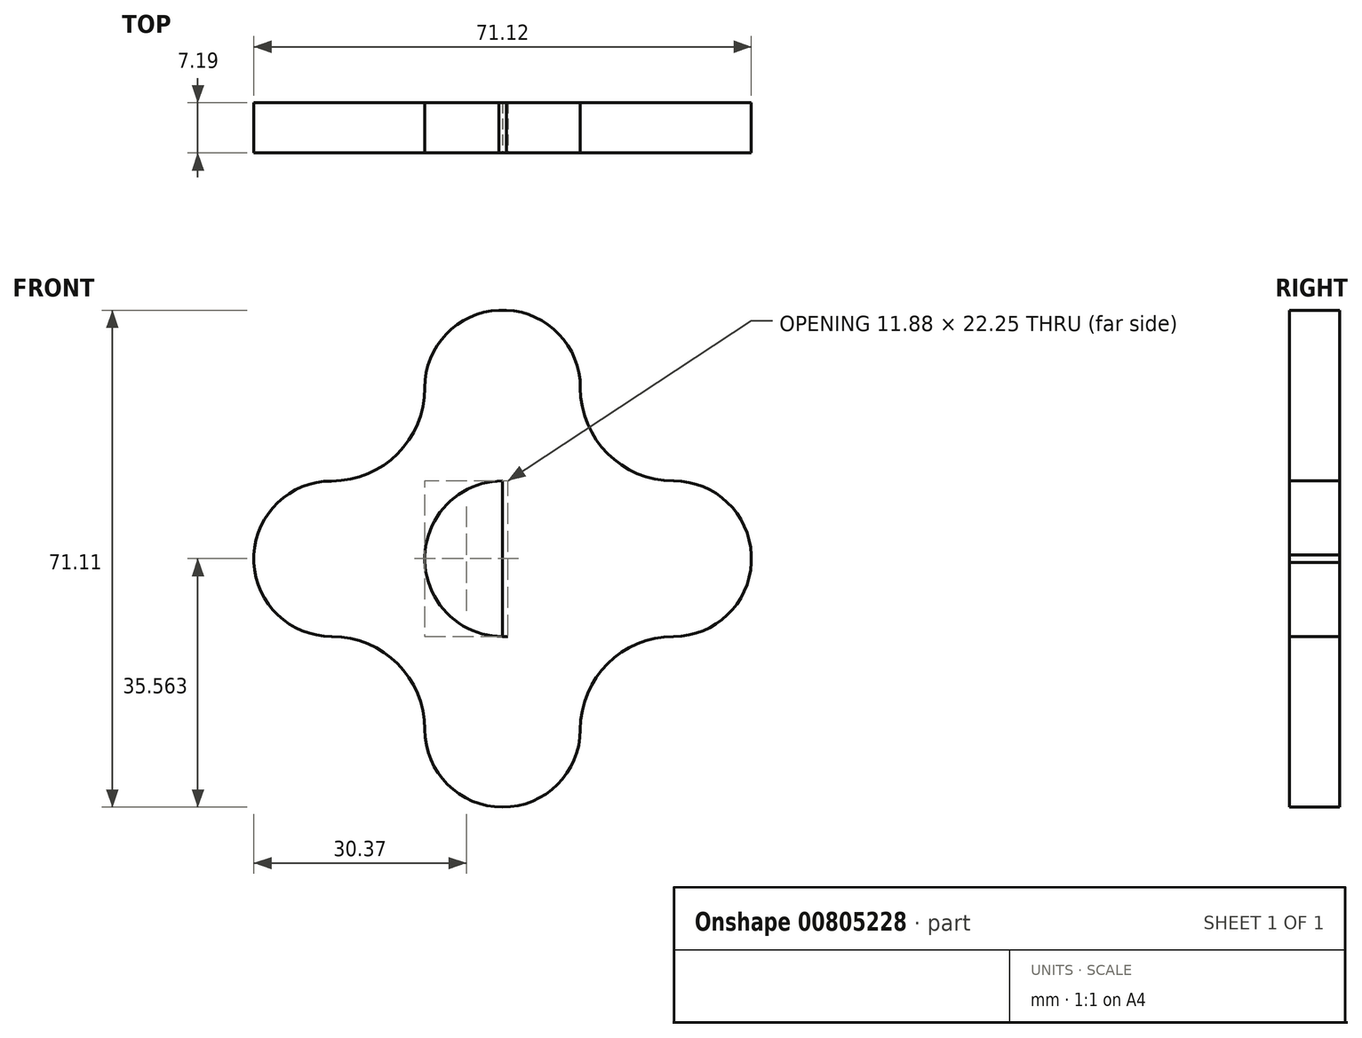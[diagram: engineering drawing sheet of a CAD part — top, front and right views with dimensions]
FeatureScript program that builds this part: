
annotation { "Feature Type Name" : "Feature", "Feature Type Description" : "" }
export const myFeature = defineFeature(function(context is Context, id is Id, definition is map)
    precondition{}
    {
        {
            var Q0;
            Q0=qCreatedBy(makeId("Front.planeOp"),FACE);
            var sketch = newSketch(context, id + "F0", { "sketchPlane" : qUnion([Q0])});
            skCircle(sketch, "E0", {"center": v(0, 0) * mm, "radius": 35.56 * mm});
            skSolve(sketch);
        }
        {
            var Q0;
            Q0=makeQuery(id+"F0.imprint","IMPRINT",FACE,{"disambiguationData":[TD([[makeQuery(id+"F0.imprint","IMPRINT",EDGE,{"derivedFrom":sQuery(id+"F0.wireOp",EDGE,"E0")}),1.0]])]});
            extrude(context, id + "F1", {"entities" : qUnion([Q0]), "depth" : 7.2 * mm, "offsetDistance" : 25.4 * mm});
        }
        {
            var Q0;
            Q0=makeQuery(id+"F1.opExtrude","CAP_FACE",FACE,{"disambiguationData":[OSD([sQuery(id+"F0.wireOp",EDGE,"E0")])],"isStart":true});
            var sketch = newSketch(context, id + "F2", { "sketchPlane" : qUnion([Q0])});
            skCircle(sketch, "E1", {"center": v(0, 0) * mm, "radius": 11.14 * mm});
            skSolve(sketch);
        }
        {
            var Q0;
            Q0=makeQuery(id+"F2.imprint","IMPRINT",FACE,{"disambiguationData":[TD([[makeQuery(id+"F2.imprint","IMPRINT",EDGE,{"derivedFrom":sQuery(id+"F2.wireOp",EDGE,"E1")}),1.0]])]});
            extrude(context, id + "F3", {"entities" : qUnion([Q0]), "operationType" : NewBodyOperationType.REMOVE, "oppositeDirection" : true, "depth" : 7.62 * mm, "offsetDistance" : 25.4 * mm});
        }
        {
            var Q0;
            Q0=makeQuery(id+"F1.opExtrude","CAP_FACE",FACE,{"disambiguationData":[OSD([sQuery(id+"F0.wireOp",EDGE,"E0")])],"isStart":false});
            var sketch = newSketch(context, id + "F4", { "sketchPlane" : qUnion([Q0])});
            skLineSegment(sketch, "E2", {"start": v(0, 35.56) * mm, "end": v(35.56, 0) * mm});
            skLineSegment(sketch, "E3", {"start": v(35.56, 0) * mm, "end": v(0, -35.56) * mm});
            skLineSegment(sketch, "E4", {"start": v(0, -35.56) * mm, "end": v(-35.56, 0) * mm});
            skLineSegment(sketch, "E5", {"start": v(-35.56, 0) * mm, "end": v(0, 35.56) * mm});
            skSolve(sketch);
        }
        {
            var Q0;
            {var subQ0=sQuery(id+"F4.wireOp",EDGE,"E4");Q0=makeQuery(id+"F4.imprint","IMPRINT",FACE,{"disambiguationData":[TD([[makeQuery(id+"F4.imprint","IMPRINT",EDGE,{"derivedFrom":subQ0}),1.0]])]});}
            var Q1;
            {var subQ0=sQuery(id+"F4.wireOp",EDGE,"E5");Q1=makeQuery(id+"F4.imprint","IMPRINT",FACE,{"disambiguationData":[TD([[makeQuery(id+"F4.imprint","IMPRINT",EDGE,{"derivedFrom":subQ0}),1.0]])]});}
            var Q2;
            {var subQ0=sQuery(id+"F4.wireOp",EDGE,"E2");Q2=makeQuery(id+"F4.imprint","IMPRINT",FACE,{"disambiguationData":[TD([[makeQuery(id+"F4.imprint","IMPRINT",EDGE,{"derivedFrom":subQ0}),1.0]])]});}
            var Q3;
            {var subQ0=sQuery(id+"F4.wireOp",EDGE,"E3");Q3=makeQuery(id+"F4.imprint","IMPRINT",FACE,{"disambiguationData":[TD([[makeQuery(id+"F4.imprint","IMPRINT",EDGE,{"derivedFrom":subQ0}),1.0]])]});}
            extrude(context, id + "F5", {"entities" : qUnion([Q0, Q1, Q2, Q3]), "operationType" : NewBodyOperationType.REMOVE, "oppositeDirection" : true, "depth" : 25.4 * mm, "offsetDistance" : 25.4 * mm});
        }
        {
            var Q0;
            Q0=makeQuery(id+"F1.opExtrude","CAP_FACE",FACE,{"disambiguationData":[OSD([sQuery(id+"F0.wireOp",EDGE,"E0")])],"isStart":false});
            var sketch = newSketch(context, id + "F6", { "sketchPlane" : qUnion([Q0])});
            skLineSegment(sketch, "E6.bottom", {"start": v(0, 11.14) * mm, "end": v(0, 11.14) * mm});
            skLineSegment(sketch, "E6.top", {"start": v(0, -11.14) * mm, "end": v(0, -11.14) * mm});
            skLineSegment(sketch, "E6.left", {"start": v(0, 11.14) * mm, "end": v(0, -11.14) * mm});
            skLineSegment(sketch, "E6.right", {"start": v(0, 11.14) * mm, "end": v(0, -11.14) * mm});
            skLineSegment(sketch, "E7.bottom", {"start": v(0, 11.14) * mm, "end": v(35.56, 11.14) * mm});
            skLineSegment(sketch, "E7.top", {"start": v(0, -11.11) * mm, "end": v(35.56, -11.11) * mm});
            skLineSegment(sketch, "E7.left", {"start": v(0, 11.14) * mm, "end": v(0, -11.11) * mm});
            skLineSegment(sketch, "E7.right", {"start": v(35.56, 11.14) * mm, "end": v(35.56, -11.11) * mm});
            skSolve(sketch);
        }
        {
            var Q0;
            {var subQ0=sQuery(id+"F6.wireOp",EDGE,"E7.right");var subQ1=sQuery(id+"F6.wireOp",EDGE,"E7.bottom");var subQ2=makeQuery(id+"F6.imprint","INTERSECT",VERTEX,{"derivedFrom":[subQ1,subQ0]});Q0=makeQuery(id+"F6.imprint","IMPRINT",FACE,{"disambiguationData":[TD([[makeQuery(id+"F6.imprint","IMPRINT",EDGE,{"disambiguationData":[TD([[subQ2,1.0]])],"derivedFrom":subQ1}),-1.0]])]});}
            var Q1;
            {var subQ0=sQuery(id+"F6.wireOp",EDGE,"E7.right");var subQ1=sQuery(id+"F6.wireOp",EDGE,"E7.top");var subQ2=makeQuery(id+"F6.imprint","INTERSECT",VERTEX,{"derivedFrom":[subQ1,subQ0]});Q1=makeQuery(id+"F6.imprint","IMPRINT",FACE,{"disambiguationData":[TD([[makeQuery(id+"F6.imprint","IMPRINT",EDGE,{"disambiguationData":[TD([[subQ2,1.0]])],"derivedFrom":subQ1}),1.0]])]});}
            var Q2;
            {var subQ0=makeQuery(id+"F5.boolean.opBoolean","COPY",EDGE,{"derivedFrom":makeQuery(id+"F5.opExtrude","CAP_EDGE",EDGE,{"disambiguationData":[OSD([sQuery(id+"F4.wireOp",EDGE,"E3")])],"isStart":true})});var subQ5=sQuery(id+"F6.wireOp",EDGE,"E7.top");var subQ6=makeQuery(id+"F6.imprint","INTERSECT",VERTEX,{"derivedFrom":[subQ0,subQ5]});Q2=makeQuery(id+"F6.imprint","IMPRINT",FACE,{"disambiguationData":[TD([[makeQuery(id+"F6.imprint","IMPRINT",EDGE,{"disambiguationData":[TD([[subQ6,1.0]])],"derivedFrom":subQ5}),1.0]])]});}
            extrude(context, id + "F7", {"entities" : qUnion([Q0, Q1, Q2]), "operationType" : NewBodyOperationType.ADD, "oppositeDirection" : true, "depth" : 7.2 * mm, "offsetDistance" : 25.4 * mm});
        }
        {
            var Q0;
            {var subQ0=sQuery(id+"F0.wireOp",EDGE,"E0");Q0=makeQuery(id+"F7.boolean.opBoolean","MERGE",FACE,{"derivedFrom":[makeQuery(id+"F1.opExtrude","CAP_FACE",FACE,{"disambiguationData":[OSD([subQ0])],"isStart":false}),makeQuery(id+"F7.opExtrude","CAP_FACE",FACE,{"disambiguationData":[OSD([subQ0,sQuery(id+"F2.wireOp",EDGE,"E1"),sQuery(id+"F6.wireOp",EDGE,"E7.bottom"),sQuery(id+"F6.wireOp",EDGE,"E7.top"),sQuery(id+"F6.wireOp",EDGE,"E7.right")])],"isStart":true})]});}
            var sketch = newSketch(context, id + "F8", { "sketchPlane" : qUnion([Q0])});
            skLineSegment(sketch, "E8.bottom", {"start": v(-11.14, 0) * mm, "end": v(11.14, 0) * mm});
            skLineSegment(sketch, "E8.top", {"start": v(-11.14, 0) * mm, "end": v(11.14, 0) * mm});
            skLineSegment(sketch, "E8.left", {"start": v(-11.14, 0) * mm, "end": v(-11.14, 0) * mm});
            skLineSegment(sketch, "E8.right", {"start": v(11.14, 0) * mm, "end": v(11.14, 0) * mm});
            skLineSegment(sketch, "E9.bottom", {"start": v(-11.14, 0) * mm, "end": v(11.11, 0) * mm});
            skLineSegment(sketch, "E9.top", {"start": v(-11.14, 35.56) * mm, "end": v(11.11, 35.56) * mm});
            skLineSegment(sketch, "E9.left", {"start": v(-11.14, 0) * mm, "end": v(-11.14, 35.56) * mm});
            skLineSegment(sketch, "E9.right", {"start": v(11.11, 0) * mm, "end": v(11.11, 35.56) * mm});
            skSolve(sketch);
        }
        {
            var Q0;
            {var subQ0=sQuery(id+"F8.wireOp",EDGE,"E9.top");var subQ3=sQuery(id+"F8.wireOp",EDGE,"E9.left");var subQ4=makeQuery(id+"F8.imprint","INTERSECT",VERTEX,{"derivedFrom":[subQ0,subQ3]});Q0=makeQuery(id+"F8.imprint","IMPRINT",FACE,{"disambiguationData":[TD([[makeQuery(id+"F8.imprint","IMPRINT",EDGE,{"disambiguationData":[TD([[subQ4,1.0]])],"derivedFrom":subQ3}),-1.0]])]});}
            var Q1;
            {var subQ0=sQuery(id+"F8.wireOp",EDGE,"E9.top");var subQ3=sQuery(id+"F8.wireOp",EDGE,"E9.right");var subQ4=makeQuery(id+"F8.imprint","INTERSECT",VERTEX,{"derivedFrom":[subQ0,subQ3]});Q1=makeQuery(id+"F8.imprint","IMPRINT",FACE,{"disambiguationData":[TD([[makeQuery(id+"F8.imprint","IMPRINT",EDGE,{"disambiguationData":[TD([[subQ4,1.0]])],"derivedFrom":subQ3}),1.0]])]});}
            var Q2;
            {var subQ3=sQuery(id+"F8.wireOp",EDGE,"E9.right");var subQ5=makeQuery(id+"F5.boolean.opBoolean","COPY",EDGE,{"derivedFrom":makeQuery(id+"F5.opExtrude","CAP_EDGE",EDGE,{"disambiguationData":[OSD([sQuery(id+"F4.wireOp",EDGE,"E2")])],"isStart":true})});var subQ6=makeQuery(id+"F8.imprint","INTERSECT",VERTEX,{"derivedFrom":[subQ5,subQ3]});Q2=makeQuery(id+"F8.imprint","IMPRINT",FACE,{"disambiguationData":[TD([[makeQuery(id+"F8.imprint","IMPRINT",EDGE,{"disambiguationData":[TD([[subQ6,1.0]])],"derivedFrom":subQ3}),1.0]])]});}
            extrude(context, id + "F9", {"entities" : qUnion([Q0, Q1, Q2]), "operationType" : NewBodyOperationType.ADD, "oppositeDirection" : true, "depth" : 7.2 * mm, "offsetDistance" : 25.4 * mm});
        }
        {
            var Q0;
            {var subQ0=sQuery(id+"F2.wireOp",EDGE,"E1");var subQ1=sQuery(id+"F0.wireOp",EDGE,"E0");Q0=makeQuery(id+"F9.boolean.opBoolean","MERGE",FACE,{"derivedFrom":[makeQuery(id+"F7.boolean.opBoolean","MERGE",FACE,{"derivedFrom":[makeQuery(id+"F1.opExtrude","CAP_FACE",FACE,{"disambiguationData":[OSD([subQ1])],"isStart":false}),makeQuery(id+"F7.opExtrude","CAP_FACE",FACE,{"disambiguationData":[OSD([subQ1,subQ0,sQuery(id+"F6.wireOp",EDGE,"E7.bottom"),sQuery(id+"F6.wireOp",EDGE,"E7.top"),sQuery(id+"F6.wireOp",EDGE,"E7.right")])],"isStart":true})]}),makeQuery(id+"F9.opExtrude","CAP_FACE",FACE,{"disambiguationData":[OSD([subQ1,subQ0,sQuery(id+"F8.wireOp",EDGE,"E9.top"),sQuery(id+"F8.wireOp",EDGE,"E9.left"),sQuery(id+"F8.wireOp",EDGE,"E9.right")])],"isStart":true})]});}
            var sketch = newSketch(context, id + "F10", { "sketchPlane" : qUnion([Q0])});
            skLineSegment(sketch, "E10.bottom", {"start": v(0, 11.14) * mm, "end": v(0, 11.14) * mm});
            skLineSegment(sketch, "E10.top", {"start": v(0, -11.14) * mm, "end": v(0, -11.14) * mm});
            skLineSegment(sketch, "E10.left", {"start": v(0, 11.14) * mm, "end": v(0, -11.14) * mm});
            skLineSegment(sketch, "E10.right", {"start": v(0, 11.14) * mm, "end": v(0, -11.14) * mm});
            skLineSegment(sketch, "E11.bottom", {"start": v(0, -11.14) * mm, "end": v(-35.56, -11.14) * mm});
            skLineSegment(sketch, "E11.top", {"start": v(0, 11.11) * mm, "end": v(-35.56, 11.11) * mm});
            skLineSegment(sketch, "E11.left", {"start": v(0, -11.14) * mm, "end": v(0, 11.11) * mm});
            skLineSegment(sketch, "E11.right", {"start": v(-35.56, -11.14) * mm, "end": v(-35.56, 11.11) * mm});
            skSolve(sketch);
        }
        {
            var Q0;
            {var subQ0=sQuery(id+"F10.wireOp",EDGE,"E11.right");var subQ1=sQuery(id+"F10.wireOp",EDGE,"E11.top");var subQ2=makeQuery(id+"F10.imprint","INTERSECT",VERTEX,{"derivedFrom":[subQ1,subQ0]});Q0=makeQuery(id+"F10.imprint","IMPRINT",FACE,{"disambiguationData":[TD([[makeQuery(id+"F10.imprint","IMPRINT",EDGE,{"disambiguationData":[TD([[subQ2,1.0]])],"derivedFrom":subQ1}),1.0]])]});}
            var Q1;
            {var subQ0=sQuery(id+"F10.wireOp",EDGE,"E11.right");var subQ1=sQuery(id+"F10.wireOp",EDGE,"E11.bottom");var subQ2=makeQuery(id+"F10.imprint","INTERSECT",VERTEX,{"derivedFrom":[subQ1,subQ0]});Q1=makeQuery(id+"F10.imprint","IMPRINT",FACE,{"disambiguationData":[TD([[makeQuery(id+"F10.imprint","IMPRINT",EDGE,{"disambiguationData":[TD([[subQ2,1.0]])],"derivedFrom":subQ1}),-1.0]])]});}
            var Q2;
            {var subQ0=makeQuery(id+"F5.boolean.opBoolean","COPY",EDGE,{"derivedFrom":makeQuery(id+"F5.opExtrude","CAP_EDGE",EDGE,{"disambiguationData":[OSD([sQuery(id+"F4.wireOp",EDGE,"E5")])],"isStart":true})});var subQ3=sQuery(id+"F10.wireOp",EDGE,"E11.top");var subQ4=makeQuery(id+"F10.imprint","INTERSECT",VERTEX,{"derivedFrom":[subQ0,subQ3]});Q2=makeQuery(id+"F10.imprint","IMPRINT",FACE,{"disambiguationData":[TD([[makeQuery(id+"F10.imprint","IMPRINT",EDGE,{"disambiguationData":[TD([[subQ4,1.0]])],"derivedFrom":subQ3}),1.0]])]});}
            extrude(context, id + "F11", {"entities" : qUnion([Q0, Q1, Q2]), "operationType" : NewBodyOperationType.ADD, "oppositeDirection" : true, "depth" : 7.2 * mm, "offsetDistance" : 25.4 * mm});
        }
        {
            var Q0;
            {var subQ0=sQuery(id+"F2.wireOp",EDGE,"E1");var subQ1=sQuery(id+"F0.wireOp",EDGE,"E0");Q0=makeQuery(id+"F11.boolean.opBoolean","MERGE",FACE,{"derivedFrom":[makeQuery(id+"F9.boolean.opBoolean","MERGE",FACE,{"derivedFrom":[makeQuery(id+"F7.boolean.opBoolean","MERGE",FACE,{"derivedFrom":[makeQuery(id+"F1.opExtrude","CAP_FACE",FACE,{"disambiguationData":[OSD([subQ1])],"isStart":false}),makeQuery(id+"F7.opExtrude","CAP_FACE",FACE,{"disambiguationData":[OSD([subQ1,subQ0,sQuery(id+"F6.wireOp",EDGE,"E7.bottom"),sQuery(id+"F6.wireOp",EDGE,"E7.top"),sQuery(id+"F6.wireOp",EDGE,"E7.right")])],"isStart":true})]}),makeQuery(id+"F9.opExtrude","CAP_FACE",FACE,{"disambiguationData":[OSD([subQ1,subQ0,sQuery(id+"F8.wireOp",EDGE,"E9.top"),sQuery(id+"F8.wireOp",EDGE,"E9.left"),sQuery(id+"F8.wireOp",EDGE,"E9.right")])],"isStart":true})]}),makeQuery(id+"F11.opExtrude","CAP_FACE",FACE,{"disambiguationData":[OSD([subQ1,subQ0,sQuery(id+"F10.wireOp",EDGE,"E11.bottom"),sQuery(id+"F10.wireOp",EDGE,"E11.top"),sQuery(id+"F10.wireOp",EDGE,"E11.right")])],"isStart":true})]});}
            var sketch = newSketch(context, id + "F12", { "sketchPlane" : qUnion([Q0])});
            skLineSegment(sketch, "E12.bottom", {"start": v(11.14, 0) * mm, "end": v(-11.14, 0) * mm});
            skLineSegment(sketch, "E12.top", {"start": v(11.14, 0) * mm, "end": v(-11.14, 0) * mm});
            skLineSegment(sketch, "E12.left", {"start": v(11.14, 0) * mm, "end": v(11.14, 0) * mm});
            skLineSegment(sketch, "E12.right", {"start": v(-11.14, 0) * mm, "end": v(-11.14, 0) * mm});
            skLineSegment(sketch, "E13.bottom", {"start": v(-11.14, 0) * mm, "end": v(11.11, 0) * mm});
            skLineSegment(sketch, "E13.top", {"start": v(-11.14, -35.56) * mm, "end": v(11.11, -35.56) * mm});
            skLineSegment(sketch, "E13.left", {"start": v(-11.14, 0) * mm, "end": v(-11.14, -35.56) * mm});
            skLineSegment(sketch, "E13.right", {"start": v(11.11, 0) * mm, "end": v(11.11, -35.56) * mm});
            skSolve(sketch);
        }
        {
            var Q0;
            {var subQ0=sQuery(id+"F12.wireOp",EDGE,"E13.top");var subQ3=sQuery(id+"F12.wireOp",EDGE,"E13.left");var subQ4=makeQuery(id+"F12.imprint","INTERSECT",VERTEX,{"derivedFrom":[subQ0,subQ3]});Q0=makeQuery(id+"F12.imprint","IMPRINT",FACE,{"disambiguationData":[TD([[makeQuery(id+"F12.imprint","IMPRINT",EDGE,{"disambiguationData":[TD([[subQ4,1.0]])],"derivedFrom":subQ3}),1.0]])]});}
            var Q1;
            {var subQ0=sQuery(id+"F12.wireOp",EDGE,"E13.top");var subQ3=sQuery(id+"F12.wireOp",EDGE,"E13.right");var subQ4=makeQuery(id+"F12.imprint","INTERSECT",VERTEX,{"derivedFrom":[subQ0,subQ3]});Q1=makeQuery(id+"F12.imprint","IMPRINT",FACE,{"disambiguationData":[TD([[makeQuery(id+"F12.imprint","IMPRINT",EDGE,{"disambiguationData":[TD([[subQ4,1.0]])],"derivedFrom":subQ3}),-1.0]])]});}
            var Q2;
            {var subQ1=makeQuery(id+"F5.boolean.opBoolean","COPY",EDGE,{"derivedFrom":makeQuery(id+"F5.opExtrude","CAP_EDGE",EDGE,{"disambiguationData":[OSD([sQuery(id+"F4.wireOp",EDGE,"E3")])],"isStart":true})});var subQ5=sQuery(id+"F12.wireOp",EDGE,"E13.right");var subQ6=makeQuery(id+"F12.imprint","INTERSECT",VERTEX,{"derivedFrom":[subQ1,subQ5]});Q2=makeQuery(id+"F12.imprint","IMPRINT",FACE,{"disambiguationData":[TD([[makeQuery(id+"F12.imprint","IMPRINT",EDGE,{"disambiguationData":[TD([[subQ6,1.0]])],"derivedFrom":subQ5}),-1.0]])]});}
            extrude(context, id + "F13", {"entities" : qUnion([Q0, Q1, Q2]), "operationType" : NewBodyOperationType.ADD, "oppositeDirection" : true, "depth" : 7.2 * mm, "offsetDistance" : 25.4 * mm});
        }
        {
            var Q0;
            {var subQ0=sQuery(id+"F2.wireOp",EDGE,"E1");var subQ1=sQuery(id+"F0.wireOp",EDGE,"E0");Q0=makeQuery(id+"F13.boolean.opBoolean","MERGE",FACE,{"derivedFrom":[makeQuery(id+"F11.boolean.opBoolean","MERGE",FACE,{"derivedFrom":[makeQuery(id+"F9.boolean.opBoolean","MERGE",FACE,{"derivedFrom":[makeQuery(id+"F7.boolean.opBoolean","MERGE",FACE,{"derivedFrom":[makeQuery(id+"F1.opExtrude","CAP_FACE",FACE,{"disambiguationData":[OSD([subQ1])],"isStart":false}),makeQuery(id+"F7.opExtrude","CAP_FACE",FACE,{"disambiguationData":[OSD([subQ1,subQ0,sQuery(id+"F6.wireOp",EDGE,"E7.bottom"),sQuery(id+"F6.wireOp",EDGE,"E7.top"),sQuery(id+"F6.wireOp",EDGE,"E7.right")])],"isStart":true})]}),makeQuery(id+"F9.opExtrude","CAP_FACE",FACE,{"disambiguationData":[OSD([subQ1,subQ0,sQuery(id+"F8.wireOp",EDGE,"E9.top"),sQuery(id+"F8.wireOp",EDGE,"E9.left"),sQuery(id+"F8.wireOp",EDGE,"E9.right")])],"isStart":true})]}),makeQuery(id+"F11.opExtrude","CAP_FACE",FACE,{"disambiguationData":[OSD([subQ1,subQ0,sQuery(id+"F10.wireOp",EDGE,"E11.bottom"),sQuery(id+"F10.wireOp",EDGE,"E11.top"),sQuery(id+"F10.wireOp",EDGE,"E11.right")])],"isStart":true})]}),makeQuery(id+"F13.opExtrude","CAP_FACE",FACE,{"disambiguationData":[OSD([subQ1,subQ0,sQuery(id+"F12.wireOp",EDGE,"E13.top"),sQuery(id+"F12.wireOp",EDGE,"E13.left"),sQuery(id+"F12.wireOp",EDGE,"E13.right")])],"isStart":true})]});}
            var sketch = newSketch(context, id + "F14", { "sketchPlane" : qUnion([Q0])});
            skArc(sketch, "E14", {"start": v(11.11, 24.45) * mm, "mid": v(-0.03, 35.57) * mm, "end": v(-11.14, 24.42) * mm});
            skArc(sketch, "E15", {"start": v(24.45, -11.11) * mm, "mid": v(35.57, 0.03) * mm, "end": v(24.42, 11.14) * mm});
            skArc(sketch, "E16", {"start": v(-11.14, -24.42) * mm, "mid": v(-0.03, -35.55) * mm, "end": v(11.11, -24.45) * mm});
            skArc(sketch, "E17", {"start": v(-24.45, 11.11) * mm, "mid": v(-35.57, -0.03) * mm, "end": v(-24.42, -11.14) * mm});
            skArc(sketch, "E18", {"start": v(11.11, 24.45) * mm, "mid": v(15.01, 15.04) * mm, "end": v(24.42, 11.14) * mm});
            skArc(sketch, "E19", {"start": v(24.45, -11.11) * mm, "mid": v(15.02, -15.02) * mm, "end": v(11.11, -24.45) * mm});
            skArc(sketch, "E20", {"start": v(-11.14, -24.42) * mm, "mid": v(-15.03, -15.03) * mm, "end": v(-24.42, -11.14) * mm});
            skArc(sketch, "E21", {"start": v(-24.45, 11.11) * mm, "mid": v(-15.04, 15.01) * mm, "end": v(-11.14, 24.42) * mm});
            skSolve(sketch);
        }
        {
            var Q0;
            Q0=makeQuery(id+"F14.imprint","IMPRINT",FACE,{"disambiguationData":[TD([[makeQuery(id+"F14.imprint","IMPRINT",EDGE,{"derivedFrom":sQuery(id+"F14.wireOp",EDGE,"E21")}),1.0]])]});
            var Q1;
            {var subQ0=sQuery(id+"F14.wireOp",EDGE,"E14");var subQ3=makeQuery(id+"F9.opExtrude","CAP_EDGE",EDGE,{"disambiguationData":[OSD([sQuery(id+"F8.wireOp",EDGE,"E9.top")])],"isStart":true});var subQ4=makeQuery(id+"F14.imprint","INTERSECT",VERTEX,{"disambiguationData":[OD(1.0)],"derivedFrom":[subQ3,subQ0]});Q1=makeQuery(id+"F14.imprint","IMPRINT",FACE,{"disambiguationData":[TD([[makeQuery(id+"F14.imprint","IMPRINT",EDGE,{"disambiguationData":[TD([[subQ4,-1.0]])],"derivedFrom":subQ0}),-1.0]])]});}
            var Q2;
            {var subQ1=makeQuery(id+"F9.opExtrude","CAP_EDGE",EDGE,{"disambiguationData":[OSD([sQuery(id+"F8.wireOp",EDGE,"E9.right")])],"isStart":true});Q2=makeQuery(id+"F14.imprint","IMPRINT",FACE,{"disambiguationData":[TD([[makeQuery(id+"F14.imprint","IMPRINT",EDGE,{"derivedFrom":subQ1}),1.0]])]});}
            var Q3;
            Q3=makeQuery(id+"F14.imprint","IMPRINT",FACE,{"disambiguationData":[TD([[makeQuery(id+"F14.imprint","IMPRINT",EDGE,{"derivedFrom":sQuery(id+"F14.wireOp",EDGE,"E18")}),1.0]])]});
            var Q4;
            {var subQ0=sQuery(id+"F14.wireOp",EDGE,"E15");var subQ3=makeQuery(id+"F7.opExtrude","CAP_EDGE",EDGE,{"disambiguationData":[OSD([sQuery(id+"F6.wireOp",EDGE,"E7.right")])],"isStart":true});var subQ4=makeQuery(id+"F14.imprint","INTERSECT",VERTEX,{"disambiguationData":[OD(1.0)],"derivedFrom":[subQ3,subQ0]});Q4=makeQuery(id+"F14.imprint","IMPRINT",FACE,{"disambiguationData":[TD([[makeQuery(id+"F14.imprint","IMPRINT",EDGE,{"disambiguationData":[TD([[subQ4,-1.0]])],"derivedFrom":subQ0}),-1.0]])]});}
            var Q5;
            {var subQ1=makeQuery(id+"F7.opExtrude","CAP_EDGE",EDGE,{"disambiguationData":[OSD([sQuery(id+"F6.wireOp",EDGE,"E7.top")])],"isStart":true});Q5=makeQuery(id+"F14.imprint","IMPRINT",FACE,{"disambiguationData":[TD([[makeQuery(id+"F14.imprint","IMPRINT",EDGE,{"derivedFrom":subQ1}),1.0]])]});}
            var Q6;
            Q6=makeQuery(id+"F14.imprint","IMPRINT",FACE,{"disambiguationData":[TD([[makeQuery(id+"F14.imprint","IMPRINT",EDGE,{"derivedFrom":sQuery(id+"F14.wireOp",EDGE,"E19")}),1.0]])]});
            var Q7;
            Q7=makeQuery(id+"F14.imprint","IMPRINT",FACE,{"disambiguationData":[TD([[makeQuery(id+"F14.imprint","IMPRINT",EDGE,{"derivedFrom":sQuery(id+"F14.wireOp",EDGE,"E16")}),-1.0]])]});
            var Q8;
            Q8=makeQuery(id+"F14.imprint","IMPRINT",FACE,{"disambiguationData":[TD([[makeQuery(id+"F14.imprint","IMPRINT",EDGE,{"derivedFrom":sQuery(id+"F14.wireOp",EDGE,"E20")}),1.0]])]});
            var Q9;
            {var subQ0=sQuery(id+"F14.wireOp",EDGE,"E17");var subQ3=makeQuery(id+"F11.opExtrude","CAP_EDGE",EDGE,{"disambiguationData":[OSD([sQuery(id+"F10.wireOp",EDGE,"E11.right")])],"isStart":true});var subQ4=makeQuery(id+"F14.imprint","INTERSECT",VERTEX,{"disambiguationData":[OD(1.0)],"derivedFrom":[subQ3,subQ0]});Q9=makeQuery(id+"F14.imprint","IMPRINT",FACE,{"disambiguationData":[TD([[makeQuery(id+"F14.imprint","IMPRINT",EDGE,{"disambiguationData":[TD([[subQ4,-1.0]])],"derivedFrom":subQ0}),-1.0]])]});}
            var Q10;
            {var subQ1=makeQuery(id+"F11.opExtrude","CAP_EDGE",EDGE,{"disambiguationData":[OSD([sQuery(id+"F10.wireOp",EDGE,"E11.top")])],"isStart":true});Q10=makeQuery(id+"F14.imprint","IMPRINT",FACE,{"disambiguationData":[TD([[makeQuery(id+"F14.imprint","IMPRINT",EDGE,{"derivedFrom":subQ1}),1.0]])]});}
            extrude(context, id + "F15", {"entities" : qUnion([Q0, Q1, Q2, Q3, Q4, Q5, Q6, Q7, Q8, Q9, Q10]), "operationType" : NewBodyOperationType.REMOVE, "oppositeDirection" : true, "depth" : 25.4 * mm, "offsetDistance" : 25.4 * mm});
        }
    });
